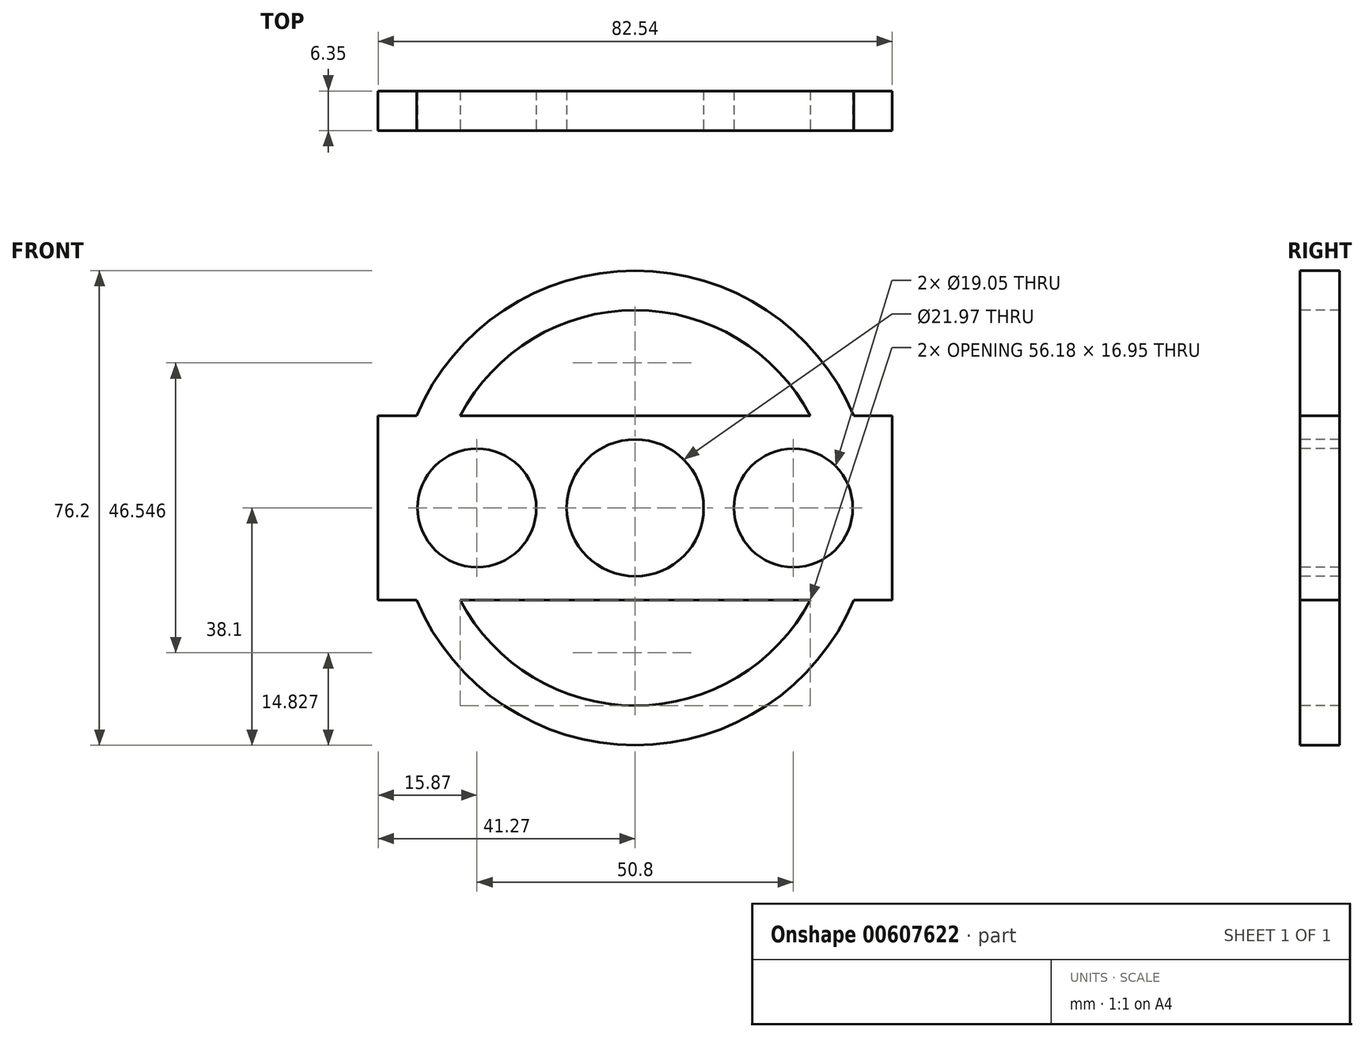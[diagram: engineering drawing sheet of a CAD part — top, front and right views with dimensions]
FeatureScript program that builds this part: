
annotation { "Feature Type Name" : "Feature", "Feature Type Description" : "" }
export const myFeature = defineFeature(function(context is Context, id is Id, definition is map)
    precondition{}
    {
        {
            var Q0;
            Q0=qCreatedBy(makeId("Front.planeOp"),FACE);
            var sketch = newSketch(context, id + "F0", { "sketchPlane" : qUnion([Q0])});
            skLineSegment(sketch, "E0.bottom", {"start": v(50.8, -50.8) * mm, "end": v(-50.8, -50.8) * mm});
            skLineSegment(sketch, "E0.top", {"start": v(50.8, 50.8) * mm, "end": v(-50.8, 50.8) * mm});
            skLineSegment(sketch, "E0.left", {"start": v(50.8, -50.8) * mm, "end": v(50.8, 50.8) * mm});
            skLineSegment(sketch, "E0.right", {"start": v(-50.8, -50.8) * mm, "end": v(-50.8, 50.8) * mm});
            skPoint(sketch, "E0.middle", {"position": v(0, 0) * mm});
            skSolve(sketch);
        }
        {
            var Q0;
            Q0 = qSketchRegion(id + "F0", true);
            extrude(context, id + "F1", {"entities" : qUnion([Q0]), "depth" : 6.35 * mm, "offsetDistance" : 25.4 * mm});
        }
        {
            var Q0;
            Q0=makeQuery(id+"F1.opExtrude","CAP_FACE",FACE,{"disambiguationData":[OSD([sQuery(id+"F0.wireOp",EDGE,"E0.bottom"),sQuery(id+"F0.wireOp",EDGE,"E0.top"),sQuery(id+"F0.wireOp",EDGE,"E0.left"),sQuery(id+"F0.wireOp",EDGE,"E0.right")])],"isStart":false});
            var sketch = newSketch(context, id + "F2", { "sketchPlane" : qUnion([Q0])});
            skCircle(sketch, "E1", {"center": v(0, 0) * mm, "radius": 10.99 * mm});
            skArc(sketch, "E2", {"start": v(-35.1, -14.8) * mm, "mid": v(0, -38.1) * mm, "end": v(35.1, -14.8) * mm});
            skArc(sketch, "E3", {"start": v(-28.1, -14.8) * mm, "mid": v(0, -31.75) * mm, "end": v(28.1, -14.8) * mm});
            skLineSegment(sketch, "E4.bottom", {"start": v(-41.27, 14.8) * mm, "end": v(41.28, 14.8) * mm});
            skLineSegment(sketch, "E4.top", {"start": v(-41.28, -14.8) * mm, "end": v(41.27, -14.8) * mm});
            skLineSegment(sketch, "E4.left", {"start": v(-41.27, 14.8) * mm, "end": v(-41.28, -14.8) * mm});
            skLineSegment(sketch, "E4.right", {"start": v(41.28, 14.8) * mm, "end": v(41.27, -14.8) * mm});
            skArc(sketch, "E5.trimOffspring", {"start": v(35.1, 14.8) * mm, "mid": v(0, 38.1) * mm, "end": v(-35.1, 14.8) * mm});
            skArc(sketch, "E6.trimOffspring", {"start": v(28.1, 14.8) * mm, "mid": v(0, 31.75) * mm, "end": v(-28.1, 14.8) * mm});
            skCircle(sketch, "E7", {"center": v(-25.4, 0) * mm, "radius": 9.53 * mm});
            skCircle(sketch, "E8", {"center": v(25.4, 0) * mm, "radius": 9.53 * mm});
            skSolve(sketch);
        }
        {
            var Q0;
            {var subQ3=sQuery(id+"F2.wireOp",EDGE,"E2");Q0=makeQuery(id+"F2.imprint","IMPRINT",FACE,{"disambiguationData":[TD([[makeQuery(id+"F2.imprint","IMPRINT",EDGE,{"derivedFrom":subQ3}),-1.0]])]});}
            var Q1;
            Q1=makeQuery(id+"F2.imprint","IMPRINT",FACE,{"disambiguationData":[TD([[makeQuery(id+"F2.imprint","IMPRINT",EDGE,{"derivedFrom":sQuery(id+"F2.wireOp",EDGE,"E7")}),1.0]])]});
            var Q2;
            Q2=makeQuery(id+"F2.imprint","IMPRINT",FACE,{"disambiguationData":[TD([[makeQuery(id+"F2.imprint","IMPRINT",EDGE,{"derivedFrom":sQuery(id+"F2.wireOp",EDGE,"E1")}),1.0]])]});
            var Q3;
            {var subQ0=sQuery(id+"F2.wireOp",EDGE,"E6.trimOffspring");Q3=makeQuery(id+"F2.imprint","IMPRINT",FACE,{"disambiguationData":[TD([[makeQuery(id+"F2.imprint","IMPRINT",EDGE,{"derivedFrom":subQ0}),1.0]])]});}
            var Q4;
            {var subQ0=sQuery(id+"F2.wireOp",EDGE,"E3");Q4=makeQuery(id+"F2.imprint","IMPRINT",FACE,{"disambiguationData":[TD([[makeQuery(id+"F2.imprint","IMPRINT",EDGE,{"derivedFrom":subQ0}),1.0]])]});}
            var Q5;
            Q5=makeQuery(id+"F2.imprint","IMPRINT",FACE,{"disambiguationData":[TD([[makeQuery(id+"F2.imprint","IMPRINT",EDGE,{"derivedFrom":sQuery(id+"F2.wireOp",EDGE,"E8")}),1.0]])]});
            extrude(context, id + "F3", {"entities" : qUnion([Q0, Q1, Q2, Q3, Q4, Q5]), "operationType" : NewBodyOperationType.REMOVE, "oppositeDirection" : true, "depth" : 25.4 * mm, "offsetDistance" : 25.4 * mm});
        }
    });
